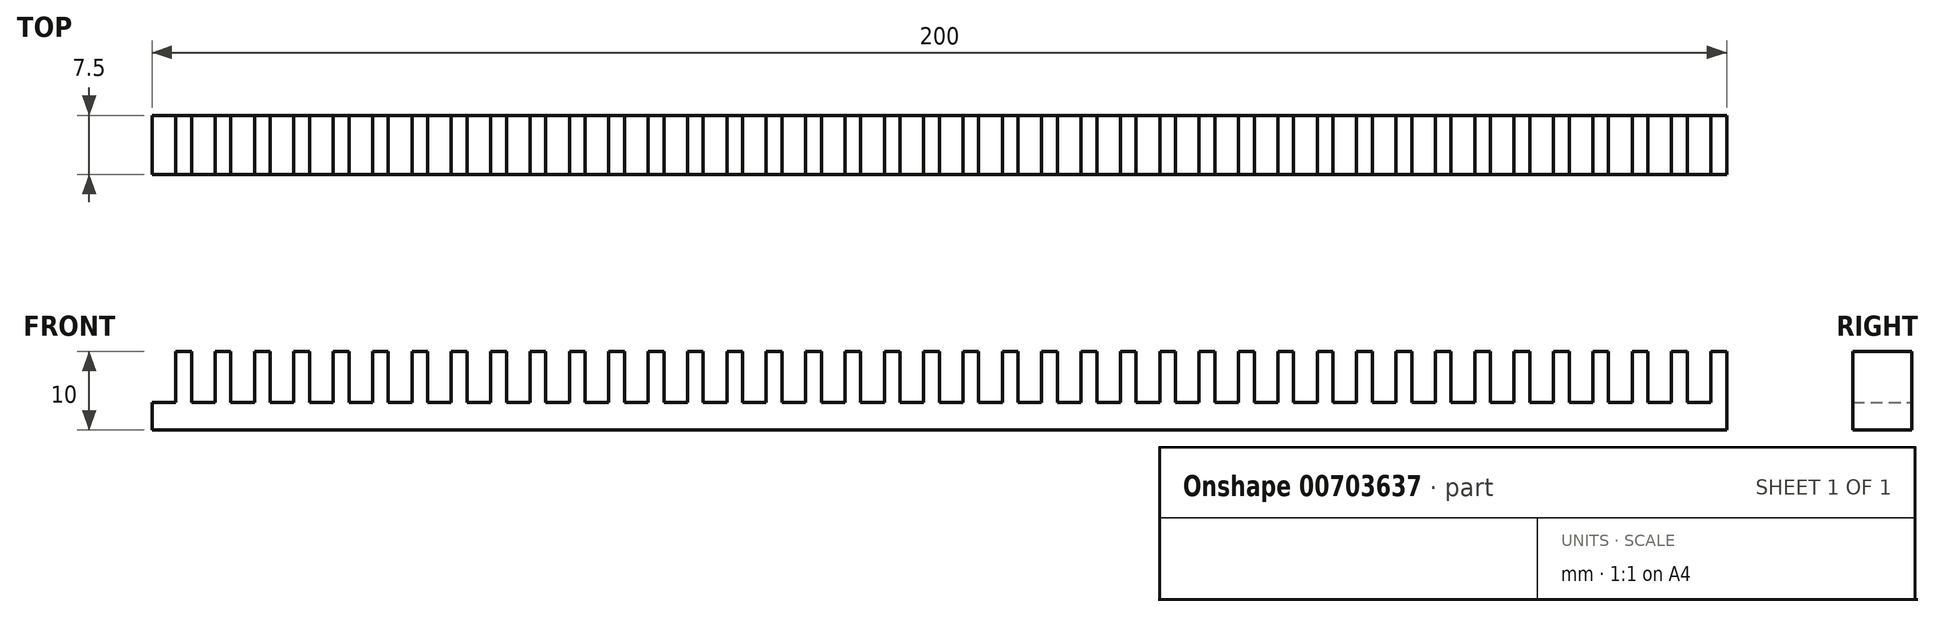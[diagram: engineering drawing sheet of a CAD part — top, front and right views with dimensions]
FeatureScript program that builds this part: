
annotation { "Feature Type Name" : "Feature", "Feature Type Description" : "" }
export const myFeature = defineFeature(function(context is Context, id is Id, definition is map)
    precondition{}
    {
        {
            var Q0;
            Q0=qCreatedBy(makeId("Top.planeOp"),FACE);
            var sketch = newSketch(context, id + "F0", { "sketchPlane" : qUnion([Q0])});
            skLineSegment(sketch, "E0.bottom", {"start": v(0, 0) * mm, "end": v(200, 0) * mm});
            skLineSegment(sketch, "E0.top", {"start": v(0, 7.5) * mm, "end": v(200, 7.5) * mm});
            skLineSegment(sketch, "E0.left", {"start": v(0, 0) * mm, "end": v(0, 7.5) * mm});
            skLineSegment(sketch, "E0.right", {"start": v(200, 0) * mm, "end": v(200, 7.5) * mm});
            skLineSegment(sketch, "E1", {"start": v(0, 0) * mm, "end": v(3, 0) * mm, "construction": true});
            skLineSegment(sketch, "E2.bottom", {"start": v(3, 0) * mm, "end": v(5, 0) * mm});
            skLineSegment(sketch, "E2.top", {"start": v(3, 7.5) * mm, "end": v(5, 7.5) * mm});
            skLineSegment(sketch, "E2.left", {"start": v(3, 0) * mm, "end": v(3, 7.5) * mm});
            skLineSegment(sketch, "E2.right", {"start": v(5, 0) * mm, "end": v(5, 7.5) * mm});
            skLineSegment(sketch, "E3.1.0.0", {"start": v(8, 0) * mm, "end": v(10, 0) * mm});
            skLineSegment(sketch, "E3.1.0.1", {"start": v(5, 0) * mm, "end": v(8, 0) * mm, "construction": true});
            skLineSegment(sketch, "E3.1.0.2", {"start": v(8, 0) * mm, "end": v(8, 7.5) * mm});
            skLineSegment(sketch, "E3.1.0.3", {"start": v(10, 0) * mm, "end": v(10, 7.5) * mm});
            skLineSegment(sketch, "E3.1.0.4", {"start": v(8, 7.5) * mm, "end": v(10, 7.5) * mm});
            skLineSegment(sketch, "E3.2.0.0", {"start": v(13, 0) * mm, "end": v(15, 0) * mm});
            skLineSegment(sketch, "E3.2.0.1", {"start": v(10, 0) * mm, "end": v(13, 0) * mm, "construction": true});
            skLineSegment(sketch, "E3.2.0.2", {"start": v(13, 0) * mm, "end": v(13, 7.5) * mm});
            skLineSegment(sketch, "E3.2.0.3", {"start": v(15, 0) * mm, "end": v(15, 7.5) * mm});
            skLineSegment(sketch, "E3.2.0.4", {"start": v(13, 7.5) * mm, "end": v(15, 7.5) * mm});
            skLineSegment(sketch, "E3.3.0.0", {"start": v(18, 0) * mm, "end": v(20, 0) * mm});
            skLineSegment(sketch, "E3.3.0.1", {"start": v(15, 0) * mm, "end": v(18, 0) * mm, "construction": true});
            skLineSegment(sketch, "E3.3.0.2", {"start": v(18, 0) * mm, "end": v(18, 7.5) * mm});
            skLineSegment(sketch, "E3.3.0.3", {"start": v(20, 0) * mm, "end": v(20, 7.5) * mm});
            skLineSegment(sketch, "E3.3.0.4", {"start": v(18, 7.5) * mm, "end": v(20, 7.5) * mm});
            skLineSegment(sketch, "E3.4.0.0", {"start": v(23, 0) * mm, "end": v(25, 0) * mm});
            skLineSegment(sketch, "E3.4.0.1", {"start": v(20, 0) * mm, "end": v(23, 0) * mm, "construction": true});
            skLineSegment(sketch, "E3.4.0.2", {"start": v(23, 0) * mm, "end": v(23, 7.5) * mm});
            skLineSegment(sketch, "E3.4.0.3", {"start": v(25, 0) * mm, "end": v(25, 7.5) * mm});
            skLineSegment(sketch, "E3.4.0.4", {"start": v(23, 7.5) * mm, "end": v(25, 7.5) * mm});
            skLineSegment(sketch, "E3.5.0.0", {"start": v(28, 0) * mm, "end": v(30, 0) * mm});
            skLineSegment(sketch, "E3.5.0.1", {"start": v(25, 0) * mm, "end": v(28, 0) * mm, "construction": true});
            skLineSegment(sketch, "E3.5.0.2", {"start": v(28, 0) * mm, "end": v(28, 7.5) * mm});
            skLineSegment(sketch, "E3.5.0.3", {"start": v(30, 0) * mm, "end": v(30, 7.5) * mm});
            skLineSegment(sketch, "E3.5.0.4", {"start": v(28, 7.5) * mm, "end": v(30, 7.5) * mm});
            skLineSegment(sketch, "E3.6.0.0", {"start": v(33, 0) * mm, "end": v(35, 0) * mm});
            skLineSegment(sketch, "E3.6.0.1", {"start": v(30, 0) * mm, "end": v(33, 0) * mm, "construction": true});
            skLineSegment(sketch, "E3.6.0.2", {"start": v(33, 0) * mm, "end": v(33, 7.5) * mm});
            skLineSegment(sketch, "E3.6.0.3", {"start": v(35, 0) * mm, "end": v(35, 7.5) * mm});
            skLineSegment(sketch, "E3.6.0.4", {"start": v(33, 7.5) * mm, "end": v(35, 7.5) * mm});
            skLineSegment(sketch, "E3.7.0.0", {"start": v(38, 0) * mm, "end": v(40, 0) * mm});
            skLineSegment(sketch, "E3.7.0.1", {"start": v(35, 0) * mm, "end": v(38, 0) * mm, "construction": true});
            skLineSegment(sketch, "E3.7.0.2", {"start": v(38, 0) * mm, "end": v(38, 7.5) * mm});
            skLineSegment(sketch, "E3.7.0.3", {"start": v(40, 0) * mm, "end": v(40, 7.5) * mm});
            skLineSegment(sketch, "E3.7.0.4", {"start": v(38, 7.5) * mm, "end": v(40, 7.5) * mm});
            skLineSegment(sketch, "E3.8.0.0", {"start": v(43, 0) * mm, "end": v(45, 0) * mm});
            skLineSegment(sketch, "E3.8.0.1", {"start": v(40, 0) * mm, "end": v(43, 0) * mm, "construction": true});
            skLineSegment(sketch, "E3.8.0.2", {"start": v(43, 0) * mm, "end": v(43, 7.5) * mm});
            skLineSegment(sketch, "E3.8.0.3", {"start": v(45, 0) * mm, "end": v(45, 7.5) * mm});
            skLineSegment(sketch, "E3.8.0.4", {"start": v(43, 7.5) * mm, "end": v(45, 7.5) * mm});
            skLineSegment(sketch, "E3.9.0.0", {"start": v(48, 0) * mm, "end": v(50, 0) * mm});
            skLineSegment(sketch, "E3.9.0.1", {"start": v(45, 0) * mm, "end": v(48, 0) * mm, "construction": true});
            skLineSegment(sketch, "E3.9.0.2", {"start": v(48, 0) * mm, "end": v(48, 7.5) * mm});
            skLineSegment(sketch, "E3.9.0.3", {"start": v(50, 0) * mm, "end": v(50, 7.5) * mm});
            skLineSegment(sketch, "E3.9.0.4", {"start": v(48, 7.5) * mm, "end": v(50, 7.5) * mm});
            skLineSegment(sketch, "E3.direction1", {"start": v(0, 0) * mm, "end": v(5, 0) * mm, "construction": true});
            skLineSegment(sketch, "E4.1.0.0", {"start": v(60, 0) * mm, "end": v(63, 0) * mm, "construction": true});
            skLineSegment(sketch, "E4.1.0.1", {"start": v(63, 0) * mm, "end": v(65, 0) * mm});
            skLineSegment(sketch, "E4.1.0.2", {"start": v(68, 0) * mm, "end": v(70, 0) * mm});
            skLineSegment(sketch, "E4.1.0.3", {"start": v(58, 7.5) * mm, "end": v(60, 7.5) * mm});
            skLineSegment(sketch, "E4.1.0.4", {"start": v(73, 0) * mm, "end": v(73, 7.5) * mm});
            skLineSegment(sketch, "E4.1.0.5", {"start": v(90, 0) * mm, "end": v(90, 7.5) * mm});
            skLineSegment(sketch, "E4.1.0.6", {"start": v(98, 0) * mm, "end": v(98, 7.5) * mm});
            skLineSegment(sketch, "E4.1.0.7", {"start": v(80, 0) * mm, "end": v(83, 0) * mm, "construction": true});
            skLineSegment(sketch, "E4.1.0.8", {"start": v(53, 7.5) * mm, "end": v(55, 7.5) * mm});
            skLineSegment(sketch, "E4.1.0.9", {"start": v(53, 0) * mm, "end": v(53, 7.5) * mm});
            skLineSegment(sketch, "E4.1.0.10", {"start": v(55, 0) * mm, "end": v(55, 7.5) * mm});
            skLineSegment(sketch, "E4.1.0.11", {"start": v(58, 0) * mm, "end": v(60, 0) * mm});
            skLineSegment(sketch, "E4.1.0.12", {"start": v(55, 0) * mm, "end": v(58, 0) * mm, "construction": true});
            skLineSegment(sketch, "E4.1.0.13", {"start": v(58, 0) * mm, "end": v(58, 7.5) * mm});
            skLineSegment(sketch, "E4.1.0.14", {"start": v(60, 0) * mm, "end": v(60, 7.5) * mm});
            skLineSegment(sketch, "E4.1.0.15", {"start": v(88, 7.5) * mm, "end": v(90, 7.5) * mm});
            skLineSegment(sketch, "E4.1.0.16", {"start": v(75, 0) * mm, "end": v(75, 7.5) * mm});
            skLineSegment(sketch, "E4.1.0.17", {"start": v(88, 0) * mm, "end": v(90, 0) * mm});
            skLineSegment(sketch, "E4.1.0.18", {"start": v(68, 7.5) * mm, "end": v(70, 7.5) * mm});
            skLineSegment(sketch, "E4.1.0.19", {"start": v(65, 0) * mm, "end": v(68, 0) * mm, "construction": true});
            skLineSegment(sketch, "E4.1.0.20", {"start": v(90, 0) * mm, "end": v(93, 0) * mm, "construction": true});
            skLineSegment(sketch, "E4.1.0.21", {"start": v(100, 0) * mm, "end": v(100, 7.5) * mm});
            skLineSegment(sketch, "E4.1.0.22", {"start": v(78, 0) * mm, "end": v(80, 0) * mm});
            skLineSegment(sketch, "E4.1.0.23", {"start": v(83, 0) * mm, "end": v(83, 7.5) * mm});
            skLineSegment(sketch, "E4.1.0.24", {"start": v(63, 0) * mm, "end": v(63, 7.5) * mm});
            skLineSegment(sketch, "E4.1.0.25", {"start": v(93, 7.5) * mm, "end": v(95, 7.5) * mm});
            skLineSegment(sketch, "E4.1.0.26", {"start": v(80, 0) * mm, "end": v(80, 7.5) * mm});
            skLineSegment(sketch, "E4.1.0.27", {"start": v(93, 0) * mm, "end": v(95, 0) * mm});
            skLineSegment(sketch, "E4.1.0.28", {"start": v(73, 7.5) * mm, "end": v(75, 7.5) * mm});
            skLineSegment(sketch, "E4.1.0.29", {"start": v(85, 0) * mm, "end": v(88, 0) * mm, "construction": true});
            skLineSegment(sketch, "E4.1.0.30", {"start": v(73, 0) * mm, "end": v(75, 0) * mm});
            skLineSegment(sketch, "E4.1.0.31", {"start": v(68, 0) * mm, "end": v(68, 7.5) * mm});
            skLineSegment(sketch, "E4.1.0.32", {"start": v(93, 0) * mm, "end": v(93, 7.5) * mm});
            skLineSegment(sketch, "E4.1.0.33", {"start": v(98, 7.5) * mm, "end": v(100, 7.5) * mm});
            skLineSegment(sketch, "E4.1.0.34", {"start": v(75, 0) * mm, "end": v(78, 0) * mm, "construction": true});
            skLineSegment(sketch, "E4.1.0.35", {"start": v(85, 0) * mm, "end": v(85, 7.5) * mm});
            skLineSegment(sketch, "E4.1.0.36", {"start": v(65, 0) * mm, "end": v(65, 7.5) * mm});
            skLineSegment(sketch, "E4.1.0.37", {"start": v(98, 0) * mm, "end": v(100, 0) * mm});
            skLineSegment(sketch, "E4.1.0.38", {"start": v(78, 7.5) * mm, "end": v(80, 7.5) * mm});
            skLineSegment(sketch, "E4.1.0.39", {"start": v(88, 0) * mm, "end": v(88, 7.5) * mm});
            skLineSegment(sketch, "E4.1.0.40", {"start": v(70, 0) * mm, "end": v(73, 0) * mm, "construction": true});
            skLineSegment(sketch, "E4.1.0.41", {"start": v(70, 0) * mm, "end": v(70, 7.5) * mm});
            skLineSegment(sketch, "E4.1.0.42", {"start": v(50, 0) * mm, "end": v(55, 0) * mm, "construction": true});
            skLineSegment(sketch, "E4.1.0.43", {"start": v(95, 0) * mm, "end": v(95, 7.5) * mm});
            skLineSegment(sketch, "E4.1.0.44", {"start": v(78, 0) * mm, "end": v(78, 7.5) * mm});
            skLineSegment(sketch, "E4.1.0.45", {"start": v(83, 7.5) * mm, "end": v(85, 7.5) * mm});
            skLineSegment(sketch, "E4.1.0.46", {"start": v(63, 7.5) * mm, "end": v(65, 7.5) * mm});
            skLineSegment(sketch, "E4.1.0.47", {"start": v(95, 0) * mm, "end": v(98, 0) * mm, "construction": true});
            skLineSegment(sketch, "E4.1.0.48", {"start": v(83, 0) * mm, "end": v(85, 0) * mm});
            skLineSegment(sketch, "E4.1.0.49", {"start": v(50, 0) * mm, "end": v(53, 0) * mm, "construction": true});
            skLineSegment(sketch, "E4.1.0.50", {"start": v(53, 0) * mm, "end": v(55, 0) * mm});
            skLineSegment(sketch, "E4.2.0.0", {"start": v(110, 0) * mm, "end": v(113, 0) * mm, "construction": true});
            skLineSegment(sketch, "E4.2.0.1", {"start": v(113, 0) * mm, "end": v(115, 0) * mm});
            skLineSegment(sketch, "E4.2.0.2", {"start": v(118, 0) * mm, "end": v(120, 0) * mm});
            skLineSegment(sketch, "E4.2.0.3", {"start": v(108, 7.5) * mm, "end": v(110, 7.5) * mm});
            skLineSegment(sketch, "E4.2.0.4", {"start": v(123, 0) * mm, "end": v(123, 7.5) * mm});
            skLineSegment(sketch, "E4.2.0.5", {"start": v(140, 0) * mm, "end": v(140, 7.5) * mm});
            skLineSegment(sketch, "E4.2.0.6", {"start": v(148, 0) * mm, "end": v(148, 7.5) * mm});
            skLineSegment(sketch, "E4.2.0.7", {"start": v(130, 0) * mm, "end": v(133, 0) * mm, "construction": true});
            skLineSegment(sketch, "E4.2.0.8", {"start": v(103, 7.5) * mm, "end": v(105, 7.5) * mm});
            skLineSegment(sketch, "E4.2.0.9", {"start": v(103, 0) * mm, "end": v(103, 7.5) * mm});
            skLineSegment(sketch, "E4.2.0.10", {"start": v(105, 0) * mm, "end": v(105, 7.5) * mm});
            skLineSegment(sketch, "E4.2.0.11", {"start": v(108, 0) * mm, "end": v(110, 0) * mm});
            skLineSegment(sketch, "E4.2.0.12", {"start": v(105, 0) * mm, "end": v(108, 0) * mm, "construction": true});
            skLineSegment(sketch, "E4.2.0.13", {"start": v(108, 0) * mm, "end": v(108, 7.5) * mm});
            skLineSegment(sketch, "E4.2.0.14", {"start": v(110, 0) * mm, "end": v(110, 7.5) * mm});
            skLineSegment(sketch, "E4.2.0.15", {"start": v(138, 7.5) * mm, "end": v(140, 7.5) * mm});
            skLineSegment(sketch, "E4.2.0.16", {"start": v(125, 0) * mm, "end": v(125, 7.5) * mm});
            skLineSegment(sketch, "E4.2.0.17", {"start": v(138, 0) * mm, "end": v(140, 0) * mm});
            skLineSegment(sketch, "E4.2.0.18", {"start": v(118, 7.5) * mm, "end": v(120, 7.5) * mm});
            skLineSegment(sketch, "E4.2.0.19", {"start": v(115, 0) * mm, "end": v(118, 0) * mm, "construction": true});
            skLineSegment(sketch, "E4.2.0.20", {"start": v(140, 0) * mm, "end": v(143, 0) * mm, "construction": true});
            skLineSegment(sketch, "E4.2.0.21", {"start": v(150, 0) * mm, "end": v(150, 7.5) * mm});
            skLineSegment(sketch, "E4.2.0.22", {"start": v(128, 0) * mm, "end": v(130, 0) * mm});
            skLineSegment(sketch, "E4.2.0.23", {"start": v(133, 0) * mm, "end": v(133, 7.5) * mm});
            skLineSegment(sketch, "E4.2.0.24", {"start": v(113, 0) * mm, "end": v(113, 7.5) * mm});
            skLineSegment(sketch, "E4.2.0.25", {"start": v(143, 7.5) * mm, "end": v(145, 7.5) * mm});
            skLineSegment(sketch, "E4.2.0.26", {"start": v(130, 0) * mm, "end": v(130, 7.5) * mm});
            skLineSegment(sketch, "E4.2.0.27", {"start": v(143, 0) * mm, "end": v(145, 0) * mm});
            skLineSegment(sketch, "E4.2.0.28", {"start": v(123, 7.5) * mm, "end": v(125, 7.5) * mm});
            skLineSegment(sketch, "E4.2.0.29", {"start": v(135, 0) * mm, "end": v(138, 0) * mm, "construction": true});
            skLineSegment(sketch, "E4.2.0.30", {"start": v(123, 0) * mm, "end": v(125, 0) * mm});
            skLineSegment(sketch, "E4.2.0.31", {"start": v(118, 0) * mm, "end": v(118, 7.5) * mm});
            skLineSegment(sketch, "E4.2.0.32", {"start": v(143, 0) * mm, "end": v(143, 7.5) * mm});
            skLineSegment(sketch, "E4.2.0.33", {"start": v(148, 7.5) * mm, "end": v(150, 7.5) * mm});
            skLineSegment(sketch, "E4.2.0.34", {"start": v(125, 0) * mm, "end": v(128, 0) * mm, "construction": true});
            skLineSegment(sketch, "E4.2.0.35", {"start": v(135, 0) * mm, "end": v(135, 7.5) * mm});
            skLineSegment(sketch, "E4.2.0.36", {"start": v(115, 0) * mm, "end": v(115, 7.5) * mm});
            skLineSegment(sketch, "E4.2.0.37", {"start": v(148, 0) * mm, "end": v(150, 0) * mm});
            skLineSegment(sketch, "E4.2.0.38", {"start": v(128, 7.5) * mm, "end": v(130, 7.5) * mm});
            skLineSegment(sketch, "E4.2.0.39", {"start": v(138, 0) * mm, "end": v(138, 7.5) * mm});
            skLineSegment(sketch, "E4.2.0.40", {"start": v(120, 0) * mm, "end": v(123, 0) * mm, "construction": true});
            skLineSegment(sketch, "E4.2.0.41", {"start": v(120, 0) * mm, "end": v(120, 7.5) * mm});
            skLineSegment(sketch, "E4.2.0.42", {"start": v(100, 0) * mm, "end": v(105, 0) * mm, "construction": true});
            skLineSegment(sketch, "E4.2.0.43", {"start": v(145, 0) * mm, "end": v(145, 7.5) * mm});
            skLineSegment(sketch, "E4.2.0.44", {"start": v(128, 0) * mm, "end": v(128, 7.5) * mm});
            skLineSegment(sketch, "E4.2.0.45", {"start": v(133, 7.5) * mm, "end": v(135, 7.5) * mm});
            skLineSegment(sketch, "E4.2.0.46", {"start": v(113, 7.5) * mm, "end": v(115, 7.5) * mm});
            skLineSegment(sketch, "E4.2.0.47", {"start": v(145, 0) * mm, "end": v(148, 0) * mm, "construction": true});
            skLineSegment(sketch, "E4.2.0.48", {"start": v(133, 0) * mm, "end": v(135, 0) * mm});
            skLineSegment(sketch, "E4.2.0.49", {"start": v(100, 0) * mm, "end": v(103, 0) * mm, "construction": true});
            skLineSegment(sketch, "E4.2.0.50", {"start": v(103, 0) * mm, "end": v(105, 0) * mm});
            skLineSegment(sketch, "E4.3.0.0", {"start": v(160, 0) * mm, "end": v(163, 0) * mm, "construction": true});
            skLineSegment(sketch, "E4.3.0.1", {"start": v(163, 0) * mm, "end": v(165, 0) * mm});
            skLineSegment(sketch, "E4.3.0.2", {"start": v(168, 0) * mm, "end": v(170, 0) * mm});
            skLineSegment(sketch, "E4.3.0.3", {"start": v(158, 7.5) * mm, "end": v(160, 7.5) * mm});
            skLineSegment(sketch, "E4.3.0.4", {"start": v(173, 0) * mm, "end": v(173, 7.5) * mm});
            skLineSegment(sketch, "E4.3.0.5", {"start": v(190, 0) * mm, "end": v(190, 7.5) * mm});
            skLineSegment(sketch, "E4.3.0.6", {"start": v(198, 0) * mm, "end": v(198, 7.5) * mm});
            skLineSegment(sketch, "E4.3.0.7", {"start": v(180, 0) * mm, "end": v(183, 0) * mm, "construction": true});
            skLineSegment(sketch, "E4.3.0.8", {"start": v(153, 7.5) * mm, "end": v(155, 7.5) * mm});
            skLineSegment(sketch, "E4.3.0.9", {"start": v(153, 0) * mm, "end": v(153, 7.5) * mm});
            skLineSegment(sketch, "E4.3.0.10", {"start": v(155, 0) * mm, "end": v(155, 7.5) * mm});
            skLineSegment(sketch, "E4.3.0.11", {"start": v(158, 0) * mm, "end": v(160, 0) * mm});
            skLineSegment(sketch, "E4.3.0.12", {"start": v(155, 0) * mm, "end": v(158, 0) * mm, "construction": true});
            skLineSegment(sketch, "E4.3.0.13", {"start": v(158, 0) * mm, "end": v(158, 7.5) * mm});
            skLineSegment(sketch, "E4.3.0.14", {"start": v(160, 0) * mm, "end": v(160, 7.5) * mm});
            skLineSegment(sketch, "E4.3.0.15", {"start": v(188, 7.5) * mm, "end": v(190, 7.5) * mm});
            skLineSegment(sketch, "E4.3.0.16", {"start": v(175, 0) * mm, "end": v(175, 7.5) * mm});
            skLineSegment(sketch, "E4.3.0.17", {"start": v(188, 0) * mm, "end": v(190, 0) * mm});
            skLineSegment(sketch, "E4.3.0.18", {"start": v(168, 7.5) * mm, "end": v(170, 7.5) * mm});
            skLineSegment(sketch, "E4.3.0.19", {"start": v(165, 0) * mm, "end": v(168, 0) * mm, "construction": true});
            skLineSegment(sketch, "E4.3.0.20", {"start": v(190, 0) * mm, "end": v(193, 0) * mm, "construction": true});
            skLineSegment(sketch, "E4.3.0.22", {"start": v(178, 0) * mm, "end": v(180, 0) * mm});
            skLineSegment(sketch, "E4.3.0.23", {"start": v(183, 0) * mm, "end": v(183, 7.5) * mm});
            skLineSegment(sketch, "E4.3.0.24", {"start": v(163, 0) * mm, "end": v(163, 7.5) * mm});
            skLineSegment(sketch, "E4.3.0.25", {"start": v(193, 7.5) * mm, "end": v(195, 7.5) * mm});
            skLineSegment(sketch, "E4.3.0.26", {"start": v(180, 0) * mm, "end": v(180, 7.5) * mm});
            skLineSegment(sketch, "E4.3.0.27", {"start": v(193, 0) * mm, "end": v(195, 0) * mm});
            skLineSegment(sketch, "E4.3.0.28", {"start": v(173, 7.5) * mm, "end": v(175, 7.5) * mm});
            skLineSegment(sketch, "E4.3.0.29", {"start": v(185, 0) * mm, "end": v(188, 0) * mm, "construction": true});
            skLineSegment(sketch, "E4.3.0.30", {"start": v(173, 0) * mm, "end": v(175, 0) * mm});
            skLineSegment(sketch, "E4.3.0.31", {"start": v(168, 0) * mm, "end": v(168, 7.5) * mm});
            skLineSegment(sketch, "E4.3.0.32", {"start": v(193, 0) * mm, "end": v(193, 7.5) * mm});
            skLineSegment(sketch, "E4.3.0.33", {"start": v(198, 7.5) * mm, "end": v(200, 7.5) * mm});
            skLineSegment(sketch, "E4.3.0.34", {"start": v(175, 0) * mm, "end": v(178, 0) * mm, "construction": true});
            skLineSegment(sketch, "E4.3.0.35", {"start": v(185, 0) * mm, "end": v(185, 7.5) * mm});
            skLineSegment(sketch, "E4.3.0.36", {"start": v(165, 0) * mm, "end": v(165, 7.5) * mm});
            skLineSegment(sketch, "E4.3.0.37", {"start": v(198, 0) * mm, "end": v(200, 0) * mm});
            skLineSegment(sketch, "E4.3.0.38", {"start": v(178, 7.5) * mm, "end": v(180, 7.5) * mm});
            skLineSegment(sketch, "E4.3.0.39", {"start": v(188, 0) * mm, "end": v(188, 7.5) * mm});
            skLineSegment(sketch, "E4.3.0.40", {"start": v(170, 0) * mm, "end": v(173, 0) * mm, "construction": true});
            skLineSegment(sketch, "E4.3.0.41", {"start": v(170, 0) * mm, "end": v(170, 7.5) * mm});
            skLineSegment(sketch, "E4.3.0.42", {"start": v(150, 0) * mm, "end": v(155, 0) * mm, "construction": true});
            skLineSegment(sketch, "E4.3.0.43", {"start": v(195, 0) * mm, "end": v(195, 7.5) * mm});
            skLineSegment(sketch, "E4.3.0.44", {"start": v(178, 0) * mm, "end": v(178, 7.5) * mm});
            skLineSegment(sketch, "E4.3.0.45", {"start": v(183, 7.5) * mm, "end": v(185, 7.5) * mm});
            skLineSegment(sketch, "E4.3.0.46", {"start": v(163, 7.5) * mm, "end": v(165, 7.5) * mm});
            skLineSegment(sketch, "E4.3.0.47", {"start": v(195, 0) * mm, "end": v(198, 0) * mm, "construction": true});
            skLineSegment(sketch, "E4.3.0.48", {"start": v(183, 0) * mm, "end": v(185, 0) * mm});
            skLineSegment(sketch, "E4.3.0.49", {"start": v(150, 0) * mm, "end": v(153, 0) * mm, "construction": true});
            skLineSegment(sketch, "E4.3.0.50", {"start": v(153, 0) * mm, "end": v(155, 0) * mm});
            skLineSegment(sketch, "E4.direction1", {"start": v(0, 0) * mm, "end": v(50, 0) * mm, "construction": true});
            skSolve(sketch);
        }
        {
            var Q0;
            {var subQ0=sQuery(id+"F0.wireOp",EDGE,"E0.left");Q0=makeQuery(id+"F0.imprint","IMPRINT",FACE,{"disambiguationData":[TD([[makeQuery(id+"F0.imprint","IMPRINT",EDGE,{"derivedFrom":subQ0}),-1.0]])]});}
            var Q1;
            {var subQ0=sQuery(id+"F0.wireOp",EDGE,"E2.right");Q1=makeQuery(id+"F0.imprint","IMPRINT",FACE,{"disambiguationData":[TD([[makeQuery(id+"F0.imprint","IMPRINT",EDGE,{"derivedFrom":subQ0}),-1.0]])]});}
            var Q2;
            {var subQ0=sQuery(id+"F0.wireOp",EDGE,"E3.1.0.3");Q2=makeQuery(id+"F0.imprint","IMPRINT",FACE,{"disambiguationData":[TD([[makeQuery(id+"F0.imprint","IMPRINT",EDGE,{"derivedFrom":subQ0}),-1.0]])]});}
            var Q3;
            {var subQ0=sQuery(id+"F0.wireOp",EDGE,"E3.2.0.3");Q3=makeQuery(id+"F0.imprint","IMPRINT",FACE,{"disambiguationData":[TD([[makeQuery(id+"F0.imprint","IMPRINT",EDGE,{"derivedFrom":subQ0}),-1.0]])]});}
            var Q4;
            {var subQ0=sQuery(id+"F0.wireOp",EDGE,"E3.3.0.3");Q4=makeQuery(id+"F0.imprint","IMPRINT",FACE,{"disambiguationData":[TD([[makeQuery(id+"F0.imprint","IMPRINT",EDGE,{"derivedFrom":subQ0}),-1.0]])]});}
            var Q5;
            {var subQ0=sQuery(id+"F0.wireOp",EDGE,"E3.4.0.3");Q5=makeQuery(id+"F0.imprint","IMPRINT",FACE,{"disambiguationData":[TD([[makeQuery(id+"F0.imprint","IMPRINT",EDGE,{"derivedFrom":subQ0}),-1.0]])]});}
            var Q6;
            {var subQ0=sQuery(id+"F0.wireOp",EDGE,"E3.5.0.3");Q6=makeQuery(id+"F0.imprint","IMPRINT",FACE,{"disambiguationData":[TD([[makeQuery(id+"F0.imprint","IMPRINT",EDGE,{"derivedFrom":subQ0}),-1.0]])]});}
            var Q7;
            {var subQ0=sQuery(id+"F0.wireOp",EDGE,"E3.6.0.3");Q7=makeQuery(id+"F0.imprint","IMPRINT",FACE,{"disambiguationData":[TD([[makeQuery(id+"F0.imprint","IMPRINT",EDGE,{"derivedFrom":subQ0}),-1.0]])]});}
            var Q8;
            {var subQ0=sQuery(id+"F0.wireOp",EDGE,"E3.7.0.3");Q8=makeQuery(id+"F0.imprint","IMPRINT",FACE,{"disambiguationData":[TD([[makeQuery(id+"F0.imprint","IMPRINT",EDGE,{"derivedFrom":subQ0}),-1.0]])]});}
            var Q9;
            {var subQ0=sQuery(id+"F0.wireOp",EDGE,"E3.8.0.3");Q9=makeQuery(id+"F0.imprint","IMPRINT",FACE,{"disambiguationData":[TD([[makeQuery(id+"F0.imprint","IMPRINT",EDGE,{"derivedFrom":subQ0}),-1.0]])]});}
            var Q10;
            {var subQ0=sQuery(id+"F0.wireOp",EDGE,"E3.9.0.3");Q10=makeQuery(id+"F0.imprint","IMPRINT",FACE,{"disambiguationData":[TD([[makeQuery(id+"F0.imprint","IMPRINT",EDGE,{"derivedFrom":subQ0}),-1.0]])]});}
            var Q11;
            {var subQ0=sQuery(id+"F0.wireOp",EDGE,"E4.1.0.10");Q11=makeQuery(id+"F0.imprint","IMPRINT",FACE,{"disambiguationData":[TD([[makeQuery(id+"F0.imprint","IMPRINT",EDGE,{"derivedFrom":subQ0}),-1.0]])]});}
            var Q12;
            {var subQ0=sQuery(id+"F0.wireOp",EDGE,"E4.1.0.14");Q12=makeQuery(id+"F0.imprint","IMPRINT",FACE,{"disambiguationData":[TD([[makeQuery(id+"F0.imprint","IMPRINT",EDGE,{"derivedFrom":subQ0}),-1.0]])]});}
            var Q13;
            {var subQ0=sQuery(id+"F0.wireOp",EDGE,"E4.1.0.31");Q13=makeQuery(id+"F0.imprint","IMPRINT",FACE,{"disambiguationData":[TD([[makeQuery(id+"F0.imprint","IMPRINT",EDGE,{"derivedFrom":subQ0}),1.0]])]});}
            var Q14;
            {var subQ0=sQuery(id+"F0.wireOp",EDGE,"E4.1.0.4");Q14=makeQuery(id+"F0.imprint","IMPRINT",FACE,{"disambiguationData":[TD([[makeQuery(id+"F0.imprint","IMPRINT",EDGE,{"derivedFrom":subQ0}),1.0]])]});}
            var Q15;
            {var subQ0=sQuery(id+"F0.wireOp",EDGE,"E4.1.0.16");Q15=makeQuery(id+"F0.imprint","IMPRINT",FACE,{"disambiguationData":[TD([[makeQuery(id+"F0.imprint","IMPRINT",EDGE,{"derivedFrom":subQ0}),-1.0]])]});}
            var Q16;
            {var subQ0=sQuery(id+"F0.wireOp",EDGE,"E4.1.0.23");Q16=makeQuery(id+"F0.imprint","IMPRINT",FACE,{"disambiguationData":[TD([[makeQuery(id+"F0.imprint","IMPRINT",EDGE,{"derivedFrom":subQ0}),1.0]])]});}
            var Q17;
            {var subQ0=sQuery(id+"F0.wireOp",EDGE,"E4.1.0.35");Q17=makeQuery(id+"F0.imprint","IMPRINT",FACE,{"disambiguationData":[TD([[makeQuery(id+"F0.imprint","IMPRINT",EDGE,{"derivedFrom":subQ0}),-1.0]])]});}
            var Q18;
            {var subQ0=sQuery(id+"F0.wireOp",EDGE,"E4.1.0.5");Q18=makeQuery(id+"F0.imprint","IMPRINT",FACE,{"disambiguationData":[TD([[makeQuery(id+"F0.imprint","IMPRINT",EDGE,{"derivedFrom":subQ0}),-1.0]])]});}
            var Q19;
            {var subQ0=sQuery(id+"F0.wireOp",EDGE,"E4.1.0.6");Q19=makeQuery(id+"F0.imprint","IMPRINT",FACE,{"disambiguationData":[TD([[makeQuery(id+"F0.imprint","IMPRINT",EDGE,{"derivedFrom":subQ0}),1.0]])]});}
            var Q20;
            {var subQ0=sQuery(id+"F0.wireOp",EDGE,"E4.1.0.21");Q20=makeQuery(id+"F0.imprint","IMPRINT",FACE,{"disambiguationData":[TD([[makeQuery(id+"F0.imprint","IMPRINT",EDGE,{"derivedFrom":subQ0}),-1.0]])]});}
            var Q21;
            {var subQ0=sQuery(id+"F0.wireOp",EDGE,"E4.2.0.10");Q21=makeQuery(id+"F0.imprint","IMPRINT",FACE,{"disambiguationData":[TD([[makeQuery(id+"F0.imprint","IMPRINT",EDGE,{"derivedFrom":subQ0}),-1.0]])]});}
            var Q22;
            {var subQ0=sQuery(id+"F0.wireOp",EDGE,"E4.2.0.14");Q22=makeQuery(id+"F0.imprint","IMPRINT",FACE,{"disambiguationData":[TD([[makeQuery(id+"F0.imprint","IMPRINT",EDGE,{"derivedFrom":subQ0}),-1.0]])]});}
            var Q23;
            {var subQ0=sQuery(id+"F0.wireOp",EDGE,"E4.2.0.31");Q23=makeQuery(id+"F0.imprint","IMPRINT",FACE,{"disambiguationData":[TD([[makeQuery(id+"F0.imprint","IMPRINT",EDGE,{"derivedFrom":subQ0}),1.0]])]});}
            var Q24;
            {var subQ0=sQuery(id+"F0.wireOp",EDGE,"E4.2.0.4");Q24=makeQuery(id+"F0.imprint","IMPRINT",FACE,{"disambiguationData":[TD([[makeQuery(id+"F0.imprint","IMPRINT",EDGE,{"derivedFrom":subQ0}),1.0]])]});}
            var Q25;
            {var subQ0=sQuery(id+"F0.wireOp",EDGE,"E4.2.0.16");Q25=makeQuery(id+"F0.imprint","IMPRINT",FACE,{"disambiguationData":[TD([[makeQuery(id+"F0.imprint","IMPRINT",EDGE,{"derivedFrom":subQ0}),-1.0]])]});}
            var Q26;
            {var subQ0=sQuery(id+"F0.wireOp",EDGE,"E4.2.0.23");Q26=makeQuery(id+"F0.imprint","IMPRINT",FACE,{"disambiguationData":[TD([[makeQuery(id+"F0.imprint","IMPRINT",EDGE,{"derivedFrom":subQ0}),1.0]])]});}
            var Q27;
            {var subQ0=sQuery(id+"F0.wireOp",EDGE,"E4.2.0.35");Q27=makeQuery(id+"F0.imprint","IMPRINT",FACE,{"disambiguationData":[TD([[makeQuery(id+"F0.imprint","IMPRINT",EDGE,{"derivedFrom":subQ0}),-1.0]])]});}
            var Q28;
            {var subQ0=sQuery(id+"F0.wireOp",EDGE,"E4.2.0.5");Q28=makeQuery(id+"F0.imprint","IMPRINT",FACE,{"disambiguationData":[TD([[makeQuery(id+"F0.imprint","IMPRINT",EDGE,{"derivedFrom":subQ0}),-1.0]])]});}
            var Q29;
            {var subQ0=sQuery(id+"F0.wireOp",EDGE,"E4.2.0.6");Q29=makeQuery(id+"F0.imprint","IMPRINT",FACE,{"disambiguationData":[TD([[makeQuery(id+"F0.imprint","IMPRINT",EDGE,{"derivedFrom":subQ0}),1.0]])]});}
            var Q30;
            {var subQ0=sQuery(id+"F0.wireOp",EDGE,"E4.2.0.21");Q30=makeQuery(id+"F0.imprint","IMPRINT",FACE,{"disambiguationData":[TD([[makeQuery(id+"F0.imprint","IMPRINT",EDGE,{"derivedFrom":subQ0}),-1.0]])]});}
            var Q31;
            {var subQ0=sQuery(id+"F0.wireOp",EDGE,"E4.3.0.10");Q31=makeQuery(id+"F0.imprint","IMPRINT",FACE,{"disambiguationData":[TD([[makeQuery(id+"F0.imprint","IMPRINT",EDGE,{"derivedFrom":subQ0}),-1.0]])]});}
            var Q32;
            {var subQ0=sQuery(id+"F0.wireOp",EDGE,"E4.3.0.14");Q32=makeQuery(id+"F0.imprint","IMPRINT",FACE,{"disambiguationData":[TD([[makeQuery(id+"F0.imprint","IMPRINT",EDGE,{"derivedFrom":subQ0}),-1.0]])]});}
            var Q33;
            {var subQ0=sQuery(id+"F0.wireOp",EDGE,"E4.3.0.31");Q33=makeQuery(id+"F0.imprint","IMPRINT",FACE,{"disambiguationData":[TD([[makeQuery(id+"F0.imprint","IMPRINT",EDGE,{"derivedFrom":subQ0}),1.0]])]});}
            var Q34;
            {var subQ0=sQuery(id+"F0.wireOp",EDGE,"E4.3.0.4");Q34=makeQuery(id+"F0.imprint","IMPRINT",FACE,{"disambiguationData":[TD([[makeQuery(id+"F0.imprint","IMPRINT",EDGE,{"derivedFrom":subQ0}),1.0]])]});}
            var Q35;
            {var subQ0=sQuery(id+"F0.wireOp",EDGE,"E4.3.0.16");Q35=makeQuery(id+"F0.imprint","IMPRINT",FACE,{"disambiguationData":[TD([[makeQuery(id+"F0.imprint","IMPRINT",EDGE,{"derivedFrom":subQ0}),-1.0]])]});}
            var Q36;
            {var subQ0=sQuery(id+"F0.wireOp",EDGE,"E4.3.0.23");Q36=makeQuery(id+"F0.imprint","IMPRINT",FACE,{"disambiguationData":[TD([[makeQuery(id+"F0.imprint","IMPRINT",EDGE,{"derivedFrom":subQ0}),1.0]])]});}
            var Q37;
            {var subQ0=sQuery(id+"F0.wireOp",EDGE,"E4.3.0.35");Q37=makeQuery(id+"F0.imprint","IMPRINT",FACE,{"disambiguationData":[TD([[makeQuery(id+"F0.imprint","IMPRINT",EDGE,{"derivedFrom":subQ0}),-1.0]])]});}
            var Q38;
            {var subQ0=sQuery(id+"F0.wireOp",EDGE,"E4.3.0.5");Q38=makeQuery(id+"F0.imprint","IMPRINT",FACE,{"disambiguationData":[TD([[makeQuery(id+"F0.imprint","IMPRINT",EDGE,{"derivedFrom":subQ0}),-1.0]])]});}
            var Q39;
            {var subQ2=sQuery(id+"F0.wireOp",EDGE,"E4.3.0.6");Q39=makeQuery(id+"F0.imprint","IMPRINT",FACE,{"disambiguationData":[TD([[makeQuery(id+"F0.imprint","IMPRINT",EDGE,{"derivedFrom":subQ2}),1.0]])]});}
            extrude(context, id + "F1", {"entities" : qUnion([Q0, Q1, Q2, Q3, Q4, Q5, Q6, Q7, Q8, Q9, Q10, Q11, Q12, Q13, Q14, Q15, Q16, Q17, Q18, Q19, Q20, Q21, Q22, Q23, Q24, Q25, Q26, Q27, Q28, Q29, Q30, Q31, Q32, Q33, Q34, Q35, Q36, Q37, Q38, Q39]), "depth" : 3.5 * mm, "offsetDistance" : 25 * mm});
        }
        {
            var Q0;
            {var subQ0=sQuery(id+"F0.wireOp",EDGE,"E2.left");Q0=makeQuery(id+"F0.imprint","IMPRINT",FACE,{"disambiguationData":[TD([[makeQuery(id+"F0.imprint","IMPRINT",EDGE,{"derivedFrom":subQ0}),-1.0]])]});}
            var Q1;
            {var subQ0=sQuery(id+"F0.wireOp",EDGE,"E3.1.0.2");Q1=makeQuery(id+"F0.imprint","IMPRINT",FACE,{"disambiguationData":[TD([[makeQuery(id+"F0.imprint","IMPRINT",EDGE,{"derivedFrom":subQ0}),-1.0]])]});}
            var Q2;
            {var subQ0=sQuery(id+"F0.wireOp",EDGE,"E3.2.0.2");Q2=makeQuery(id+"F0.imprint","IMPRINT",FACE,{"disambiguationData":[TD([[makeQuery(id+"F0.imprint","IMPRINT",EDGE,{"derivedFrom":subQ0}),-1.0]])]});}
            var Q3;
            {var subQ0=sQuery(id+"F0.wireOp",EDGE,"E3.3.0.2");Q3=makeQuery(id+"F0.imprint","IMPRINT",FACE,{"disambiguationData":[TD([[makeQuery(id+"F0.imprint","IMPRINT",EDGE,{"derivedFrom":subQ0}),-1.0]])]});}
            var Q4;
            {var subQ0=sQuery(id+"F0.wireOp",EDGE,"E3.4.0.2");Q4=makeQuery(id+"F0.imprint","IMPRINT",FACE,{"disambiguationData":[TD([[makeQuery(id+"F0.imprint","IMPRINT",EDGE,{"derivedFrom":subQ0}),-1.0]])]});}
            var Q5;
            {var subQ0=sQuery(id+"F0.wireOp",EDGE,"E3.5.0.2");Q5=makeQuery(id+"F0.imprint","IMPRINT",FACE,{"disambiguationData":[TD([[makeQuery(id+"F0.imprint","IMPRINT",EDGE,{"derivedFrom":subQ0}),-1.0]])]});}
            var Q6;
            {var subQ0=sQuery(id+"F0.wireOp",EDGE,"E3.6.0.2");Q6=makeQuery(id+"F0.imprint","IMPRINT",FACE,{"disambiguationData":[TD([[makeQuery(id+"F0.imprint","IMPRINT",EDGE,{"derivedFrom":subQ0}),-1.0]])]});}
            var Q7;
            {var subQ0=sQuery(id+"F0.wireOp",EDGE,"E3.7.0.2");Q7=makeQuery(id+"F0.imprint","IMPRINT",FACE,{"disambiguationData":[TD([[makeQuery(id+"F0.imprint","IMPRINT",EDGE,{"derivedFrom":subQ0}),-1.0]])]});}
            var Q8;
            {var subQ0=sQuery(id+"F0.wireOp",EDGE,"E3.8.0.2");Q8=makeQuery(id+"F0.imprint","IMPRINT",FACE,{"disambiguationData":[TD([[makeQuery(id+"F0.imprint","IMPRINT",EDGE,{"derivedFrom":subQ0}),-1.0]])]});}
            var Q9;
            {var subQ2=sQuery(id+"F0.wireOp",EDGE,"E3.9.0.2");Q9=makeQuery(id+"F0.imprint","IMPRINT",FACE,{"disambiguationData":[TD([[makeQuery(id+"F0.imprint","IMPRINT",EDGE,{"derivedFrom":subQ2}),-1.0]])]});}
            var Q10;
            {var subQ0=sQuery(id+"F0.wireOp",EDGE,"E4.1.0.9");Q10=makeQuery(id+"F0.imprint","IMPRINT",FACE,{"disambiguationData":[TD([[makeQuery(id+"F0.imprint","IMPRINT",EDGE,{"derivedFrom":subQ0}),-1.0]])]});}
            var Q11;
            {var subQ0=sQuery(id+"F0.wireOp",EDGE,"E4.1.0.13");Q11=makeQuery(id+"F0.imprint","IMPRINT",FACE,{"disambiguationData":[TD([[makeQuery(id+"F0.imprint","IMPRINT",EDGE,{"derivedFrom":subQ0}),-1.0]])]});}
            var Q12;
            {var subQ0=sQuery(id+"F0.wireOp",EDGE,"E4.1.0.24");Q12=makeQuery(id+"F0.imprint","IMPRINT",FACE,{"disambiguationData":[TD([[makeQuery(id+"F0.imprint","IMPRINT",EDGE,{"derivedFrom":subQ0}),-1.0]])]});}
            var Q13;
            {var subQ0=sQuery(id+"F0.wireOp",EDGE,"E4.1.0.31");Q13=makeQuery(id+"F0.imprint","IMPRINT",FACE,{"disambiguationData":[TD([[makeQuery(id+"F0.imprint","IMPRINT",EDGE,{"derivedFrom":subQ0}),-1.0]])]});}
            var Q14;
            {var subQ0=sQuery(id+"F0.wireOp",EDGE,"E4.1.0.4");Q14=makeQuery(id+"F0.imprint","IMPRINT",FACE,{"disambiguationData":[TD([[makeQuery(id+"F0.imprint","IMPRINT",EDGE,{"derivedFrom":subQ0}),-1.0]])]});}
            var Q15;
            {var subQ0=sQuery(id+"F0.wireOp",EDGE,"E4.1.0.26");Q15=makeQuery(id+"F0.imprint","IMPRINT",FACE,{"disambiguationData":[TD([[makeQuery(id+"F0.imprint","IMPRINT",EDGE,{"derivedFrom":subQ0}),1.0]])]});}
            var Q16;
            {var subQ0=sQuery(id+"F0.wireOp",EDGE,"E4.1.0.23");Q16=makeQuery(id+"F0.imprint","IMPRINT",FACE,{"disambiguationData":[TD([[makeQuery(id+"F0.imprint","IMPRINT",EDGE,{"derivedFrom":subQ0}),-1.0]])]});}
            var Q17;
            {var subQ0=sQuery(id+"F0.wireOp",EDGE,"E4.1.0.5");Q17=makeQuery(id+"F0.imprint","IMPRINT",FACE,{"disambiguationData":[TD([[makeQuery(id+"F0.imprint","IMPRINT",EDGE,{"derivedFrom":subQ0}),1.0]])]});}
            var Q18;
            {var subQ0=sQuery(id+"F0.wireOp",EDGE,"E4.1.0.32");Q18=makeQuery(id+"F0.imprint","IMPRINT",FACE,{"disambiguationData":[TD([[makeQuery(id+"F0.imprint","IMPRINT",EDGE,{"derivedFrom":subQ0}),-1.0]])]});}
            var Q19;
            {var subQ0=sQuery(id+"F0.wireOp",EDGE,"E4.1.0.6");Q19=makeQuery(id+"F0.imprint","IMPRINT",FACE,{"disambiguationData":[TD([[makeQuery(id+"F0.imprint","IMPRINT",EDGE,{"derivedFrom":subQ0}),-1.0]])]});}
            var Q20;
            {var subQ0=sQuery(id+"F0.wireOp",EDGE,"E4.2.0.9");Q20=makeQuery(id+"F0.imprint","IMPRINT",FACE,{"disambiguationData":[TD([[makeQuery(id+"F0.imprint","IMPRINT",EDGE,{"derivedFrom":subQ0}),-1.0]])]});}
            var Q21;
            {var subQ0=sQuery(id+"F0.wireOp",EDGE,"E4.2.0.13");Q21=makeQuery(id+"F0.imprint","IMPRINT",FACE,{"disambiguationData":[TD([[makeQuery(id+"F0.imprint","IMPRINT",EDGE,{"derivedFrom":subQ0}),-1.0]])]});}
            var Q22;
            {var subQ0=sQuery(id+"F0.wireOp",EDGE,"E4.2.0.24");Q22=makeQuery(id+"F0.imprint","IMPRINT",FACE,{"disambiguationData":[TD([[makeQuery(id+"F0.imprint","IMPRINT",EDGE,{"derivedFrom":subQ0}),-1.0]])]});}
            var Q23;
            {var subQ0=sQuery(id+"F0.wireOp",EDGE,"E4.2.0.31");Q23=makeQuery(id+"F0.imprint","IMPRINT",FACE,{"disambiguationData":[TD([[makeQuery(id+"F0.imprint","IMPRINT",EDGE,{"derivedFrom":subQ0}),-1.0]])]});}
            var Q24;
            {var subQ0=sQuery(id+"F0.wireOp",EDGE,"E4.2.0.4");Q24=makeQuery(id+"F0.imprint","IMPRINT",FACE,{"disambiguationData":[TD([[makeQuery(id+"F0.imprint","IMPRINT",EDGE,{"derivedFrom":subQ0}),-1.0]])]});}
            var Q25;
            {var subQ0=sQuery(id+"F0.wireOp",EDGE,"E4.2.0.26");Q25=makeQuery(id+"F0.imprint","IMPRINT",FACE,{"disambiguationData":[TD([[makeQuery(id+"F0.imprint","IMPRINT",EDGE,{"derivedFrom":subQ0}),1.0]])]});}
            var Q26;
            {var subQ0=sQuery(id+"F0.wireOp",EDGE,"E4.2.0.23");Q26=makeQuery(id+"F0.imprint","IMPRINT",FACE,{"disambiguationData":[TD([[makeQuery(id+"F0.imprint","IMPRINT",EDGE,{"derivedFrom":subQ0}),-1.0]])]});}
            var Q27;
            {var subQ0=sQuery(id+"F0.wireOp",EDGE,"E4.2.0.5");Q27=makeQuery(id+"F0.imprint","IMPRINT",FACE,{"disambiguationData":[TD([[makeQuery(id+"F0.imprint","IMPRINT",EDGE,{"derivedFrom":subQ0}),1.0]])]});}
            var Q28;
            {var subQ0=sQuery(id+"F0.wireOp",EDGE,"E4.2.0.32");Q28=makeQuery(id+"F0.imprint","IMPRINT",FACE,{"disambiguationData":[TD([[makeQuery(id+"F0.imprint","IMPRINT",EDGE,{"derivedFrom":subQ0}),-1.0]])]});}
            var Q29;
            {var subQ0=sQuery(id+"F0.wireOp",EDGE,"E4.2.0.6");Q29=makeQuery(id+"F0.imprint","IMPRINT",FACE,{"disambiguationData":[TD([[makeQuery(id+"F0.imprint","IMPRINT",EDGE,{"derivedFrom":subQ0}),-1.0]])]});}
            var Q30;
            {var subQ0=sQuery(id+"F0.wireOp",EDGE,"E4.3.0.9");Q30=makeQuery(id+"F0.imprint","IMPRINT",FACE,{"disambiguationData":[TD([[makeQuery(id+"F0.imprint","IMPRINT",EDGE,{"derivedFrom":subQ0}),-1.0]])]});}
            var Q31;
            {var subQ0=sQuery(id+"F0.wireOp",EDGE,"E4.3.0.13");Q31=makeQuery(id+"F0.imprint","IMPRINT",FACE,{"disambiguationData":[TD([[makeQuery(id+"F0.imprint","IMPRINT",EDGE,{"derivedFrom":subQ0}),-1.0]])]});}
            var Q32;
            {var subQ0=sQuery(id+"F0.wireOp",EDGE,"E4.3.0.24");Q32=makeQuery(id+"F0.imprint","IMPRINT",FACE,{"disambiguationData":[TD([[makeQuery(id+"F0.imprint","IMPRINT",EDGE,{"derivedFrom":subQ0}),-1.0]])]});}
            var Q33;
            {var subQ0=sQuery(id+"F0.wireOp",EDGE,"E4.3.0.31");Q33=makeQuery(id+"F0.imprint","IMPRINT",FACE,{"disambiguationData":[TD([[makeQuery(id+"F0.imprint","IMPRINT",EDGE,{"derivedFrom":subQ0}),-1.0]])]});}
            var Q34;
            {var subQ0=sQuery(id+"F0.wireOp",EDGE,"E4.3.0.4");Q34=makeQuery(id+"F0.imprint","IMPRINT",FACE,{"disambiguationData":[TD([[makeQuery(id+"F0.imprint","IMPRINT",EDGE,{"derivedFrom":subQ0}),-1.0]])]});}
            var Q35;
            {var subQ0=sQuery(id+"F0.wireOp",EDGE,"E4.3.0.26");Q35=makeQuery(id+"F0.imprint","IMPRINT",FACE,{"disambiguationData":[TD([[makeQuery(id+"F0.imprint","IMPRINT",EDGE,{"derivedFrom":subQ0}),1.0]])]});}
            var Q36;
            {var subQ0=sQuery(id+"F0.wireOp",EDGE,"E4.3.0.23");Q36=makeQuery(id+"F0.imprint","IMPRINT",FACE,{"disambiguationData":[TD([[makeQuery(id+"F0.imprint","IMPRINT",EDGE,{"derivedFrom":subQ0}),-1.0]])]});}
            var Q37;
            {var subQ0=sQuery(id+"F0.wireOp",EDGE,"E4.3.0.5");Q37=makeQuery(id+"F0.imprint","IMPRINT",FACE,{"disambiguationData":[TD([[makeQuery(id+"F0.imprint","IMPRINT",EDGE,{"derivedFrom":subQ0}),1.0]])]});}
            var Q38;
            {var subQ2=sQuery(id+"F0.wireOp",EDGE,"E4.3.0.32");Q38=makeQuery(id+"F0.imprint","IMPRINT",FACE,{"disambiguationData":[TD([[makeQuery(id+"F0.imprint","IMPRINT",EDGE,{"derivedFrom":subQ2}),-1.0]])]});}
            var Q39;
            {var subQ0=sQuery(id+"F0.wireOp",EDGE,"E0.right");Q39=makeQuery(id+"F0.imprint","IMPRINT",FACE,{"disambiguationData":[TD([[makeQuery(id+"F0.imprint","IMPRINT",EDGE,{"derivedFrom":subQ0}),1.0]])]});}
            extrude(context, id + "F2", {"entities" : qUnion([Q0, Q1, Q2, Q3, Q4, Q5, Q6, Q7, Q8, Q9, Q10, Q11, Q12, Q13, Q14, Q15, Q16, Q17, Q18, Q19, Q20, Q21, Q22, Q23, Q24, Q25, Q26, Q27, Q28, Q29, Q30, Q31, Q32, Q33, Q34, Q35, Q36, Q37, Q38, Q39]), "operationType" : NewBodyOperationType.ADD, "depth" : 10 * mm, "offsetDistance" : 25 * mm});
        }
    });
